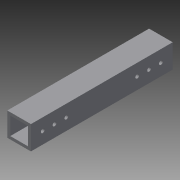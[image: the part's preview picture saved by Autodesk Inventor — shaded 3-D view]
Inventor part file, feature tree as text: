
AUTODESK INVENTOR PART (.ipt)
format: ipt  version: 2014 (Build 180170000, 170)  size: 98,304 bytes
history: native  units: in
note: dims shown in document units (in); Inventor stores cm internally (conversion verified against a paired STEP export)
features: extrude x2, sketch x2
ambient origin geometry x8: Origin, YZ Plane, XZ Plane, XY Plane, X Axis, Y Axis, Z Axis, Center Point
bodies: Solid1 (feature_tree)
feature tree (4):
  extrude  "Extrusion1"  Depth=1.0in
  extrude  "Extrusion2"  Depth=6.0in TaperAngle=0.0deg
  sketch  "Sketch1"  dims[d0=1.0in d1=1.0in]
  sketch  "Sketch2"  dims[d3=0.125in d4=6.0in d5=0.0in d6=0.163in d7=0.5in d8=0.5in d9=1.1811in d11=0.5in d12=0.3937in d14=1.0in d16=6.0in d17=0.0in]
